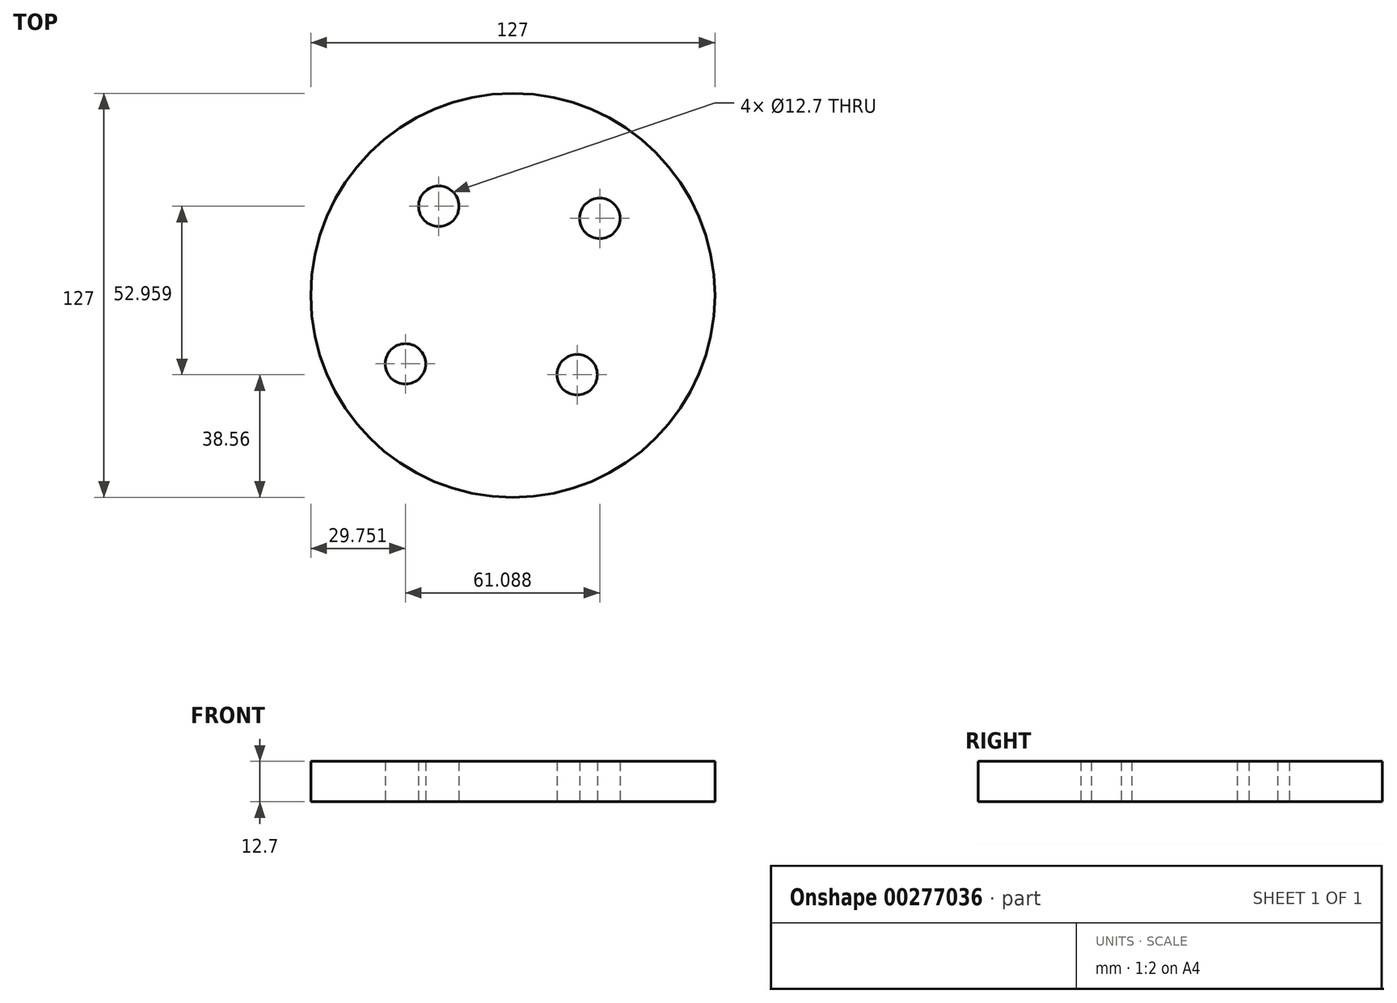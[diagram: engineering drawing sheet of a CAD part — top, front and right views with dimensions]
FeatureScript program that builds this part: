
annotation { "Feature Type Name" : "Feature", "Feature Type Description" : "" }
export const myFeature = defineFeature(function(context is Context, id is Id, definition is map)
    precondition{}
    {
        {
            var Q0;
            Q0=qCreatedBy(makeId("Top.planeOp"),FACE);
            var sketch = newSketch(context, id + "F0", { "sketchPlane" : qUnion([Q0])});
            skCircle(sketch, "E0", {"center": v(-80.54, 13.4) * mm, "radius": 63.5 * mm});
            skCircle(sketch, "E1", {"center": v(-114.29, -8.13) * mm, "radius": 6.35 * mm});
            skCircle(sketch, "E2", {"center": v(-103.8, 41.43) * mm, "radius": 6.35 * mm});
            skCircle(sketch, "E3", {"center": v(-53.2, 37.63) * mm, "radius": 6.35 * mm});
            skCircle(sketch, "E4", {"center": v(-60.32, -11.53) * mm, "radius": 6.35 * mm});
            skSolve(sketch);
        }
        {
            var Q0;
            Q0 = qSketchRegion(id + "F0", true);
            extrude(context, id + "F1", {"entities" : qUnion([Q0]), "depth" : 12.7 * mm});
        }
    });
